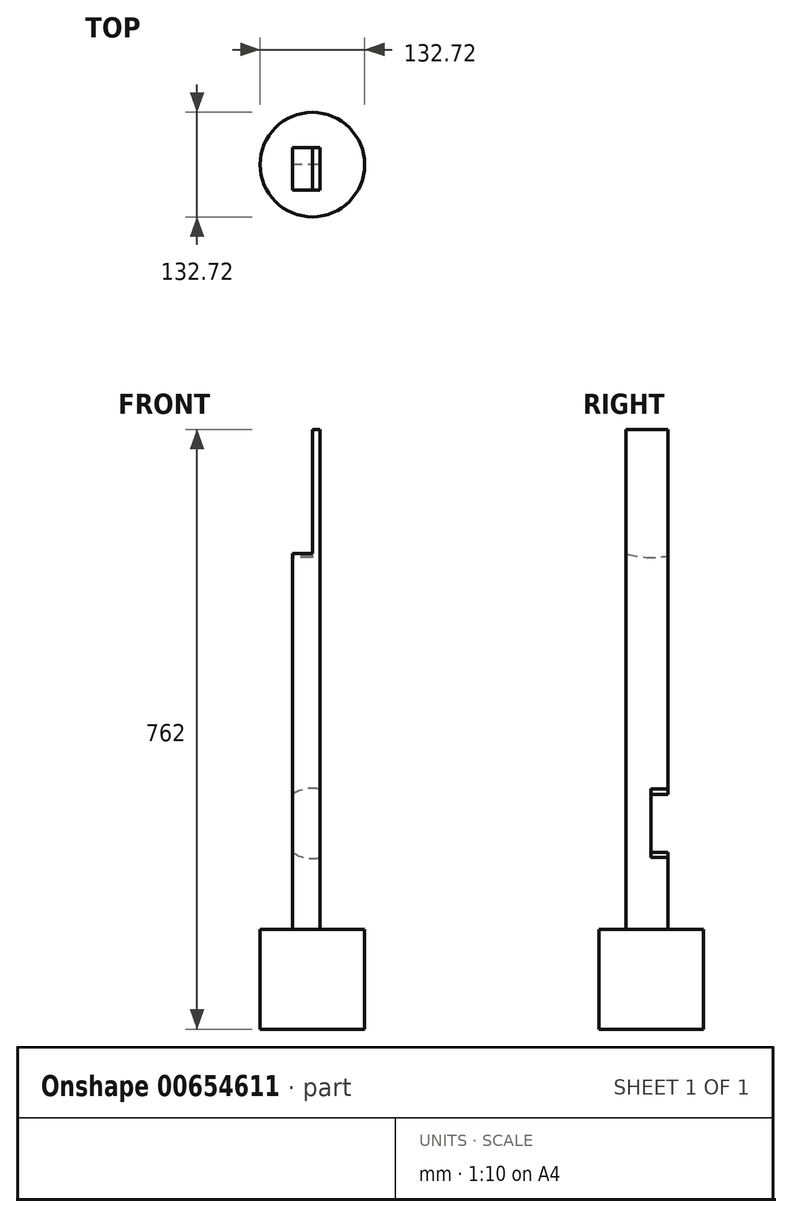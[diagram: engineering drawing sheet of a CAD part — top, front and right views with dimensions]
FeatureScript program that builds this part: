
annotation { "Feature Type Name" : "Feature", "Feature Type Description" : "" }
export const myFeature = defineFeature(function(context is Context, id is Id, definition is map)
    precondition{}
    {
        {
            var Q0;
            Q0=qCreatedBy(makeId("Top.planeOp"),FACE);
            var sketch = newSketch(context, id + "F0", { "sketchPlane" : qUnion([Q0])});
            skCircle(sketch, "E0", {"center": v(0, 0) * mm, "radius": 66.36 * mm});
            skSolve(sketch);
        }
        {
            var Q0;
            Q0 = qSketchRegion(id + "F0", true);
            extrude(context, id + "F1", {"entities" : qUnion([Q0]), "depth" : 101.6 * mm, "offsetDistance" : 25.4 * mm});
        }
        {
            var Q0;
            Q0=makeQuery(id+"F1.opExtrude","CAP_FACE",FACE,{"disambiguationData":[OSD([sQuery(id+"F0.wireOp",EDGE,"E0")])],"isStart":false});
            extrude(context, id + "F2", {"entities" : qUnion([Q0]), "operationType" : NewBodyOperationType.ADD, "depth" : 25.4 * mm, "offsetDistance" : 25.4 * mm});
        }
        {
            var Q0;
            Q0=makeQuery(id+"F2.opExtrude","CAP_FACE",FACE,{"disambiguationData":[OSD([sQuery(id+"F0.wireOp",EDGE,"E0")])],"isStart":false});
            var sketch = newSketch(context, id + "F3", { "sketchPlane" : qUnion([Q0])});
            skLineSegment(sketch, "E1.bottom", {"start": v(0, 21.41) * mm, "end": v(9.64, 21.41) * mm});
            skLineSegment(sketch, "E1.top", {"start": v(0, -32.16) * mm, "end": v(9.64, -32.16) * mm});
            skLineSegment(sketch, "E1.left", {"start": v(0, 21.41) * mm, "end": v(0, -32.16) * mm});
            skLineSegment(sketch, "E1.right", {"start": v(9.64, 21.41) * mm, "end": v(9.64, -32.16) * mm});
            skPoint(sketch, "E1.middle", {"position": v(4.82, -5.37) * mm});
            skSolve(sketch);
        }
        {
            var Q0;
            Q0 = qSketchRegion(id + "F3", true);
            extrude(context, id + "F4", {"entities" : qUnion([Q0]), "operationType" : NewBodyOperationType.ADD, "depth" : 635 * mm, "offsetDistance" : 25.4 * mm});
        }
        {
            var Q0;
            Q0=makeQuery(id+"F4.opExtrude","SWEPT_FACE",FACE,{"disambiguationData":[OSD([sQuery(id+"F3.wireOp",EDGE,"E1.left")])]});
            extrude(context, id + "F5", {"entities" : qUnion([Q0]), "operationType" : NewBodyOperationType.ADD, "depth" : 25.4 * mm, "offsetDistance" : 25.4 * mm});
        }
        {
            var Q0;
            Q0=makeQuery(id+"F5.opExtrude","CAP_FACE",FACE,{"disambiguationData":[OSD([sQuery(id+"F3.wireOp",EDGE,"E1.left")])],"isStart":false});
            var sketch = newSketch(context, id + "F6", { "sketchPlane" : qUnion([Q0])});
            skCircle(sketch, "E2", {"center": v(-10.75, 506.18) * mm, "radius": 35.33 * mm});
            skSolve(sketch);
        }
        {
            var Q0;
            Q0=sQuery(id+"F6.wireOp",EDGE,"E2");
            extrude(context, id + "F7", {"bodyType" : ToolBodyType.SURFACE, "surfaceEntities" : qUnion([Q0]), "depth" : 254 * mm, "offsetDistance" : 25.4 * mm});
        }
        {
            var Q0;
            Q0=makeQuery(id+"F5.opExtrude","CAP_FACE",FACE,{"disambiguationData":[OSD([sQuery(id+"F3.wireOp",EDGE,"E1.left")])],"isStart":false});
            var sketch = newSketch(context, id + "F8", { "sketchPlane" : qUnion([Q0])});
            skCircle(sketch, "E3", {"center": v(0, 708.84) * mm, "radius": 109.52 * mm});
            skSolve(sketch);
        }
        {
            var Q0;
            {var subQ1=sQuery(id+"F3.wireOp",EDGE,"E1.left");var subQ6=makeQuery(id+"F5.opExtrude","CAP_EDGE",EDGE,{"disambiguationData":[OSD([subQ1]),TDD([makeQuery(id+"F4.opExtrude","CAP_EDGE",EDGE,{"disambiguationData":[OSD([subQ1])],"isStart":false})])],"isStart":false});Q0=makeQuery(id+"F8.imprint","IMPRINT",FACE,{"disambiguationData":[TD([[makeQuery(id+"F8.imprint","IMPRINT",EDGE,{"derivedFrom":subQ6}),-1.0]])]});}
            var Q1;
            {var subQ1=sQuery(id+"F3.wireOp",EDGE,"E1.left");var subQ6=makeQuery(id+"F5.opExtrude","CAP_EDGE",EDGE,{"disambiguationData":[OSD([subQ1]),TDD([makeQuery(id+"F4.opExtrude","CAP_EDGE",EDGE,{"disambiguationData":[OSD([subQ1])],"isStart":false})])],"isStart":false});Q1=makeQuery(id+"F8.imprint","IMPRINT",FACE,{"disambiguationData":[TD([[makeQuery(id+"F8.imprint","IMPRINT",EDGE,{"derivedFrom":subQ6}),1.0]])]});}
            extrude(context, id + "F9", {"entities" : qUnion([Q0, Q1]), "operationType" : NewBodyOperationType.REMOVE, "oppositeDirection" : true, "depth" : 25.4 * mm, "offsetDistance" : 25.4 * mm});
        }
        {
            var Q0;
            Q0=qCreatedBy(makeId("Front.planeOp"),FACE);
            var sketch = newSketch(context, id + "F10", { "sketchPlane" : qUnion([Q0])});
            skCircle(sketch, "E4", {"center": v(0, 261.49) * mm, "radius": 44.57 * mm});
            skSolve(sketch);
        }
        {
            var Q0;
            Q0 = qSketchRegion(id + "F10", true);
            extrude(context, id + "F11", {"entities" : qUnion([Q0]), "operationType" : NewBodyOperationType.REMOVE, "oppositeDirection" : true, "depth" : 25.4 * mm, "offsetDistance" : 25.4 * mm});
        }
    });
